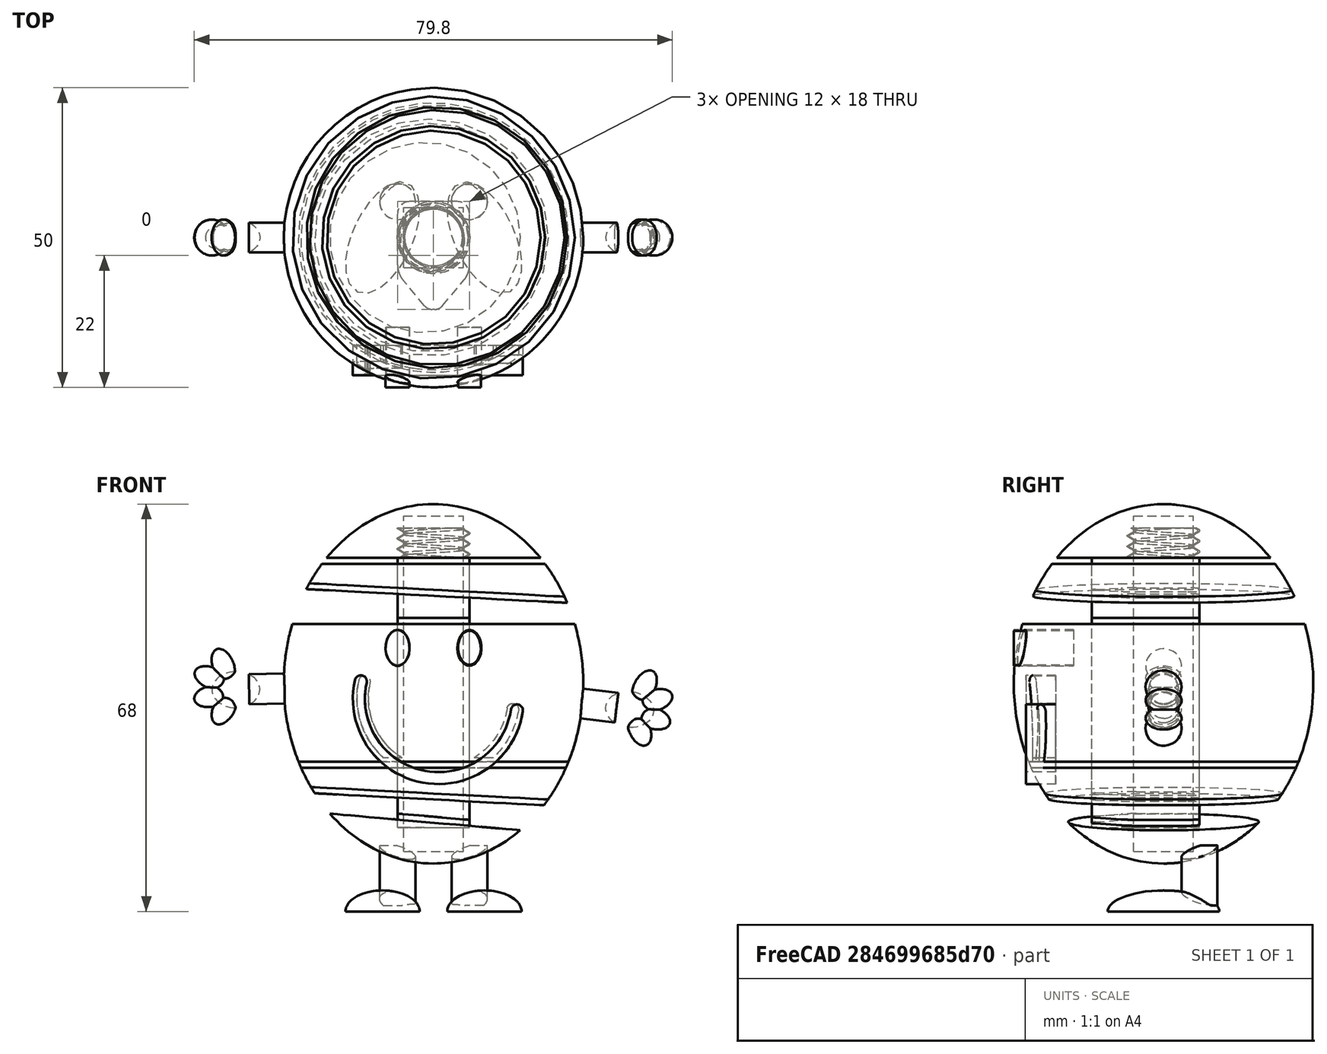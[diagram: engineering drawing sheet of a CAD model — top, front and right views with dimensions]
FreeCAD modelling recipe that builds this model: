
FCSTD DOCUMENT  (FreeCAD 0.21R33771 (Git))
Label: Mr Bump v2
License: All rights reserved
LicenseURL: http://en.wikipedia.org/wiki/All_rights_reserved
objects: Part::FeaturePython×45, Part::Plane×12, Part::MultiFuse×11, Part::Ellipsoid×7, App::DocumentObjectGroup×6, Part::Mirroring×3, Part::Extrusion×3, Part::Box×2, Part::Cylinder×2, Sketcher::SketchObject×2, Part::Part2DObjectPython×2, Part::Face×1, Part::Offset2D×1, Part::Wedge×1, Part::Fillet×1
note: 93 computed .brp shape members not serialized (recipe doc carries the construction recipe); baked Part::Feature solids carry a one-line shape summary decoded from their .brp

FEATURE [Part::Ellipsoid] Ellipsoid
  Angle1 = -90
  Angle2 = 90
  Angle3 = 360
  AttacherType = Attacher::AttachEngine3D
  Radius1 = 30
  Radius2 = 25
  Radius3 = 25
FEATURE [Part::Box] Box  label="Cube"
  AttacherType = Attacher::AttachEngine3D
  Height = 56
  Length = 10
  Placement = pos=(-5,-5,-28) rot=(0,0,1;0rad)
  Width = 10
FEATURE [Part::Cylinder] Cylinder
  Angle = 360
  AttacherType = Attacher::AttachEngine3D
  FirstAngle = 0
  Height = 10
  Placement = pos=(6,6,-37) rot=(0,0,1;0rad)
  Radius = 3
  SecondAngle = 0
FEATURE [Part::Ellipsoid] Ellipsoid006
  Angle1 = -90
  Angle2 = 90
  Angle3 = 360
  AttacherType = Attacher::AttachEngine3D
  Placement = pos=(8.5,0,-38) rot=(0,0,1;0.436332rad)
  Radius1 = 3.5
  Radius2 = 5
  Radius3 = 10
FEATURE [Sketcher::SketchObject] Sketch012
  FullyConstrained = false
  sketch-geometry (4):
    g0: LineSegment StartX=-75.9093 StartY=70.947 StartZ=0 EndX=76.7827 EndY=70.947 EndZ=0
    g1: LineSegment StartX=76.7827 StartY=70.947 StartZ=0 EndX=76.7827 EndY=-70.9765 EndZ=0
    g2: LineSegment StartX=76.7827 StartY=-70.9765 StartZ=0 EndX=-75.9093 EndY=-70.9765 EndZ=0
    g3: LineSegment StartX=-75.9093 StartY=-70.9765 StartZ=0 EndX=-75.9093 EndY=70.947 EndZ=0
  constraints (8):
    c: Coincident(g0,g1)
    c: Coincident(g1,g2)
    c: Coincident(g2,g3)
    c: Coincident(g3,g0)
    c: Horizontal(g0)
    c: Horizontal(g2)
    c: Vertical(g1)
    c: Vertical(g3)
FEATURE [Part::Face] Face012
  FaceMakerClass = Part::FaceMakerBullseye
  Placement = pos=(-7,0,-38) rot=(0,0,1;0rad)
  Sources = -> [Sketch012]
FEATURE [Part::FeaturePython] Slice  # WARN: FeaturePython — macro-defined, semantics opaque (R4)
  Base = -> Ellipsoid006
  Mode = 1
  Tolerance = 0
  Tools = -> [Face012]
FEATURE [Part::FeaturePython] Slice_child0  label="Slice.0"  # WARN: FeaturePython — macro-defined, semantics opaque (R4)
  Base = -> Slice
  FilterType = 1
  Invert = false
  OverrideMaxVal = 0
  WindowFrom = 80
  WindowTo = 100
  items = 0
FEATURE [Part::MultiFuse] Fusion  label="Foot"
  Shapes = -> [Slice_child0,Cylinder]
FEATURE [Part::Cylinder] Cylinder002
  Angle = 360
  AttacherType = Attacher::AttachEngine3D
  FirstAngle = 0
  Height = 8
  Placement = pos=(26,0,0) rot=(0,1,0;1.5708rad)
  Radius = 2.5
  SecondAngle = 0
FEATURE [Part::Ellipsoid] Ellipsoid001
  Angle1 = -90
  Angle2 = 90
  Angle3 = 360
  AttacherType = Attacher::AttachEngine3D
  Placement = pos=(35,0,0) rot=(0,0,1;0rad)
  Radius1 = 3
  Radius2 = 4
  Radius3 = 3
FEATURE [Part::Ellipsoid] Ellipsoid002
  Angle1 = -90
  Angle2 = 90
  Angle3 = 360
  AttacherType = Attacher::AttachEngine3D
  Placement = pos=(37,0,4) rot=(0,1,0;0.349066rad)
  Radius1 = 3
  Radius2 = 1.75
  Radius3 = 3
FEATURE [Part::Ellipsoid] Ellipsoid003
  Angle1 = -90
  Angle2 = 90
  Angle3 = 360
  AttacherType = Attacher::AttachEngine3D
  Placement = pos=(39,0,2) rot=(0,1,0;1.13446rad)
  Radius1 = 3
  Radius2 = 1.75
  Radius3 = 3
FEATURE [Part::Ellipsoid] Ellipsoid004
  Angle1 = -90
  Angle2 = 90
  Angle3 = 360
  AttacherType = Attacher::AttachEngine3D
  Placement = pos=(39,0,-1) rot=(0,1,0;1.74533rad)
  Radius1 = 3
  Radius2 = 1.75
  Radius3 = 3
FEATURE [Part::Ellipsoid] Ellipsoid005
  Angle1 = -90
  Angle2 = 90
  Angle3 = 360
  AttacherType = Attacher::AttachEngine3D
  Placement = pos=(37,0,-3) rot=(0,-1,0;0.523599rad)
  Radius1 = 3
  Radius2 = 1.75
  Radius3 = 3
FEATURE [Part::MultiFuse] Fusion002  label="Hand"
  Placement = pos=(-2,0,0) rot=(0,1,0;0.122173rad)
  Shapes = -> [Cylinder002,Ellipsoid001,Ellipsoid002,Ellipsoid003,Ellipsoid004,Ellipsoid005]
FEATURE [Part::Mirroring] Part__Mirroring  label="Foot (Mirror #1)"
  Base = (1,0,0)
  Normal = (1,0,0)
  Placement = pos=(-2,0,0) rot=(0,0,1;0rad)
  Source = -> Fusion
FEATURE [Part::MultiFuse] Fusion003  label="Feet"
  Shapes = -> [Part__Mirroring,Fusion]
FEATURE [Part::Mirroring] Part__Mirroring001  label="Hand (Mirror #2)"
  Base = (0,0,0)
  Normal = (1,0,-0.05)
  Source = -> Fusion002
FEATURE [Part::MultiFuse] Fusion004  label="Hands"
  Shapes = -> [Fusion002,Part__Mirroring001]
FEATURE [Part::Part2DObjectPython] Ellipse001  # Draft 2D object (typed FeaturePython)
  Area = 18.8496
  FirstAngle = 0
  LastAngle = 0
  MajorRadius = 3
  MakeFace = true
  MinorRadius = 2
  Placement = pos=(6,0,6) rot=(0.57735,-0.57735,0.57735;2.0944rad)
FEATURE [Part::Extrusion] Extrude002  label="Eye Hole Right"
  Base = -> Ellipse001
  Dir = (-1e-16,-1,3e-16)
  DirMode = 2
  FaceMakerClass = Part::FaceMakerBullseye
  LengthFwd = 10
  LengthRev = 0
  Placement = pos=(0,-15,0) rot=(0,0,1;0rad)
  Solid = false
  Symmetric = false
FEATURE [Part::FeaturePython] Clone  label="Uncut Eye"  # Draft clone (typed FeaturePython)
  AttacherType = Attacher::AttachEngine3D
  Fuse = false
  Objects = -> [Extrude002]
  Placement = pos=(0.3,-15,0.3) rot=(0,0,1;0rad)
  Scale = (0.95,1,0.95)
FEATURE [Part::Part2DObjectPython] Ellipse002  # Draft 2D object (typed FeaturePython)
  Area = 18.8496
  FirstAngle = 0
  LastAngle = 0
  MajorRadius = 3
  MakeFace = true
  MinorRadius = 2
  Placement = pos=(7,0,6) rot=(0.57735,-0.57735,0.57735;2.0944rad)
FEATURE [Part::Extrusion] Extrude003  label="Eye Hole Left"
  Base = -> Ellipse002
  Dir = (-2e-16,-1,2e-16)
  DirMode = 2
  FaceMakerClass = Part::FaceMakerBullseye
  LengthFwd = 10
  LengthRev = 0
  Placement = pos=(-13,-15,0) rot=(0,0,1;0rad)
  Solid = false
  Symmetric = false
FEATURE [Sketcher::SketchObject] Sketch005
  FullyConstrained = false
  Placement = pos=(0,0,0) rot=(1,0,0;1.5708rad)
  sketch-geometry (1):
    g0: ArcOfCircle CenterX=0.810583 CenterY=-2.47492 CenterZ=0 NormalX=0 NormalY=0 NormalZ=1 AngleXU=0 Radius=13.2658 StartAngle=2.92236 EndAngle=6.13423
FEATURE [Part::Offset2D] Offset2D
  Fill = false
  Intersection = false
  Join = 0
  Mode = 1
  SelfIntersection = false
  Source = -> Sketch005
  Value = 1
FEATURE [Part::Extrusion] Extrude  label="Mouth Hole"
  Base = -> Offset2D
  Dir = (0,1,-2e-16)
  DirMode = 2
  FaceMakerClass = Part::FaceMakerBullseye
  LengthFwd = 5
  LengthRev = 0
  Placement = pos=(0,-23,0) rot=(0,0,1;0rad)
  Solid = true
  Symmetric = false
FEATURE [Part::Plane] Plane
  AttacherType = Attacher::AttachEngine3D
  Length = 50
  Placement = pos=(-25,-25,-13) rot=(0,0,1;0rad)
  Width = 50
FEATURE [Part::Plane] Plane001
  AttacherType = Attacher::AttachEngine3D
  Length = 50
  Placement = pos=(-25,-25,-14) rot=(0,0,1;0rad)
  Width = 50
FEATURE [Part::Plane] Plane002
  AttacherType = Attacher::AttachEngine3D
  Length = 50
  Placement = pos=(-25,-25,-17) rot=(0,1,0;0.05236rad)
  Width = 50
FEATURE [Part::Plane] Plane003
  AttacherType = Attacher::AttachEngine3D
  Length = 50
  Placement = pos=(-25,-25,-18) rot=(0,1,0;0.05236rad)
  Width = 50
FEATURE [Part::Plane] Plane004
  AttacherType = Attacher::AttachEngine3D
  Length = 50
  Placement = pos=(-25,-25,-20) rot=(0,1,0;0.087266rad)
  Width = 50
FEATURE [Part::Plane] Plane005
  AttacherType = Attacher::AttachEngine3D
  Length = 50
  Placement = pos=(-25,-25,-21) rot=(0,1,0;0.087266rad)
  Width = 50
FEATURE [Part::Plane] Plane006
  AttacherType = Attacher::AttachEngine3D
  Length = 50
  Placement = pos=(-25,-25,10) rot=(0,0,1;0rad)
  Width = 50
FEATURE [Part::Plane] Plane007
  AttacherType = Attacher::AttachEngine3D
  Length = 50
  Placement = pos=(-25,-25,11) rot=(0,0,1;0rad)
  Width = 50
FEATURE [Part::Plane] Plane008
  AttacherType = Attacher::AttachEngine3D
  Length = 50
  Placement = pos=(-25,-25,17) rot=(0,1,0;0.05236rad)
  Width = 50
FEATURE [Part::Plane] Plane009
  AttacherType = Attacher::AttachEngine3D
  Length = 50
  Placement = pos=(-25,-25,16) rot=(0,1,0;0.05236rad)
  Width = 50
FEATURE [Part::Plane] Plane010
  AttacherType = Attacher::AttachEngine3D
  Length = 50
  Placement = pos=(-25,-25,21) rot=(0,0,1;0rad)
  Width = 50
FEATURE [Part::Plane] Plane011
  AttacherType = Attacher::AttachEngine3D
  Length = 50
  Placement = pos=(-25,-25,20) rot=(0,0,1;0rad)
  Width = 50
FEATURE [Part::Box] Box001  label="Cube001"
  AttacherType = Attacher::AttachEngine3D
  Height = 45
  Length = 12
  Placement = pos=(-6,-6,-24) rot=(0,0,1;0rad)
  Width = 12
FEATURE [Part::FeaturePython] ScrewTap  label="M12x5-ScrewTap"  # Fasteners workbench fastener (typed FeaturePython)
  Placement = pos=(0,0,26) rot=(0,0,1;0rad)
  diameter = 11
  diameterCustom = 6
  invert = false
  leftHanded = false
  length = 5
  matchOuter = false
  offset = 0
  pitchCustom = 1
  thread = true
  type = 2
FEATURE [Part::FeaturePython] Clone001  label="Mouth Right"  # WARN: FeaturePython — macro-defined, semantics opaque (R4)
  AttacherType = Attacher::AttachEngine3D
  Fuse = false
  Scale = (0.95,1,0.95)
FEATURE [Part::FeaturePython] Clone002  label="Mouth Left"  # WARN: FeaturePython — macro-defined, semantics opaque (R4)
  AttacherType = Attacher::AttachEngine3D
  Fuse = false
  Scale = (0.95,1,0.95)
FEATURE [Part::FeaturePython] Slice004  # WARN: FeaturePython — macro-defined, semantics opaque (R4)
  Base = -> Clone
  Mode = 1
  Tolerance = 0
  Tools = -> [Ellipsoid]
FEATURE [Part::FeaturePython] Slice004_child0  label="Eye Right"  # WARN: FeaturePython — macro-defined, semantics opaque (R4)
  Base = -> Slice004
  FilterType = 1
  Invert = false
  OverrideMaxVal = 0
  WindowFrom = 80
  WindowTo = 100
  items = 0
FEATURE [Part::FeaturePython] Slice004_child1  label="Slice004.1"  # WARN: FeaturePython — macro-defined, semantics opaque (R4)
  Base = -> Slice004
  FilterType = 1
  Invert = false
  OverrideMaxVal = 0
  WindowFrom = 80
  WindowTo = 100
  items = 1
FEATURE [App::DocumentObjectGroup] GrExplode_Slice004  label="Exploded Slice004"
  Group = -> [Slice004_child1]
FEATURE [App::DocumentObjectGroup] GrExplode_Slice005  label="Exploded Slice005"
FEATURE [Part::Mirroring] Part__Mirroring002  label="Eye Left"
  Base = (0,0,0)
  Normal = (1,0,0)
  Source = -> Slice004_child0
FEATURE [Part::Wedge] Wedge
  AttacherType = Attacher::AttachEngine3D
  Placement = pos=(0,-12,0) rot=(0,0,1;0rad)
  X2max = 6
  X2min = -6
  Xmax = 1
  Xmin = -1
  Ymax = 6
  Ymin = 0
  Z2max = 21
  Z2min = -24
  Zmax = 21
  Zmin = -24
FEATURE [Part::MultiFuse] Fusion010
  Shapes = -> [Wedge,Box001]
FEATURE [Part::Fillet] Fillet
  Base = -> Fusion010
  Edges = 6 edges: [Edge1 r=1.75,Edge3 r=4,Edge6 r=1.75,Edge11 r=2,Edge15 r=4,Edge19 r=2]
FEATURE [Part::MultiFuse] Fusion011  label="Threaded Prismoid"
  Shapes = -> [Fillet,ScrewTap]
FEATURE [Part::FeaturePython] Slice005  # WARN: FeaturePython — macro-defined, semantics opaque (R4)
  Base = -> Ellipsoid
  Mode = 1
  Tolerance = 0
  Tools = -> [Plane011,Extrude002,Extrude003,Extrude,Plane,Plane001,Plane002,Plane003,Plane004,Plane005,Plane006,Plane007,Plane008,Plane009,Plane010,Fusion011]
FEATURE [Part::FeaturePython] Slice005_child0  label="White Bandage 5"  # WARN: FeaturePython — macro-defined, semantics opaque (R4)
  Base = -> Slice005
  FilterType = 1
  Invert = false
  OverrideMaxVal = 0
  WindowFrom = 80
  WindowTo = 100
  items = 0
FEATURE [Part::FeaturePython] Slice005_child1  label="Black Bandage 6"  # WARN: FeaturePython — macro-defined, semantics opaque (R4)
  Base = -> Slice005
  FilterType = 1
  Invert = false
  OverrideMaxVal = 0
  WindowFrom = 80
  WindowTo = 100
  items = 1
FEATURE [Part::FeaturePython] Slice005_child2  label="White Bandage 4"  # WARN: FeaturePython — macro-defined, semantics opaque (R4)
  Base = -> Slice005
  FilterType = 1
  Invert = false
  OverrideMaxVal = 0
  WindowFrom = 80
  WindowTo = 100
  items = 2
FEATURE [Part::FeaturePython] Slice005_child3  label="Slice005.3"  # WARN: FeaturePython — macro-defined, semantics opaque (R4)
  Base = -> Slice005
  FilterType = 1
  Invert = false
  OverrideMaxVal = 0
  WindowFrom = 80
  WindowTo = 100
  items = 3
FEATURE [Part::FeaturePython] Slice005_child4  label="Black Bandage 5"  # WARN: FeaturePython — macro-defined, semantics opaque (R4)
  Base = -> Slice005
  FilterType = 1
  Invert = false
  OverrideMaxVal = 0
  WindowFrom = 80
  WindowTo = 100
  items = 4
FEATURE [Part::FeaturePython] Slice005_child5  label="Slice005.x001"  # WARN: FeaturePython — macro-defined, semantics opaque (R4)
  Base = -> Slice005
  FilterType = 1
  Invert = false
  OverrideMaxVal = 0
  WindowFrom = 80
  WindowTo = 100
  items = 5
FEATURE [Part::FeaturePython] Slice005_child6  label="Slice005.6"  # WARN: FeaturePython — macro-defined, semantics opaque (R4)
  Base = -> Slice005
  FilterType = 1
  Invert = false
  OverrideMaxVal = 0
  WindowFrom = 80
  WindowTo = 100
  items = 6
FEATURE [Part::FeaturePython] Slice005_child7  label="White Bandage 3"  # WARN: FeaturePython — macro-defined, semantics opaque (R4)
  Base = -> Slice005
  FilterType = 1
  Invert = false
  OverrideMaxVal = 0
  WindowFrom = 80
  WindowTo = 100
  items = 7
FEATURE [Part::FeaturePython] Slice005_child8  label="Slice005.8"  # WARN: FeaturePython — macro-defined, semantics opaque (R4)
  Base = -> Slice005
  FilterType = 1
  Invert = false
  OverrideMaxVal = 0
  WindowFrom = 80
  WindowTo = 100
  items = 8
FEATURE [Part::FeaturePython] Slice005_child9  label="Black Bandage 4"  # WARN: FeaturePython — macro-defined, semantics opaque (R4)
  Base = -> Slice005
  FilterType = 1
  Invert = false
  OverrideMaxVal = 0
  WindowFrom = 80
  WindowTo = 100
  items = 9
FEATURE [Part::FeaturePython] Slice005_child10  label="Slice005.10"  # WARN: FeaturePython — macro-defined, semantics opaque (R4)
  Base = -> Slice005
  FilterType = 1
  Invert = false
  OverrideMaxVal = 0
  WindowFrom = 80
  WindowTo = 100
  items = 10
FEATURE [Part::FeaturePython] Slice005_child11  label="Slice005.11"  # WARN: FeaturePython — macro-defined, semantics opaque (R4)
  Base = -> Slice005
  FilterType = 1
  Invert = false
  OverrideMaxVal = 0
  WindowFrom = 80
  WindowTo = 100
  items = 11
FEATURE [Part::MultiFuse] Fusion008  label="Face and Hands"
  Shapes = -> [Fusion004,Slice005_child11]
FEATURE [Part::FeaturePython] Slice005_child12  label="Slice005.12"  # WARN: FeaturePython — macro-defined, semantics opaque (R4)
  Base = -> Slice005
  FilterType = 1
  Invert = false
  OverrideMaxVal = 0
  WindowFrom = 80
  WindowTo = 100
  items = 12
FEATURE [Part::FeaturePython] Slice005_child13  label="Slice005.13"  # WARN: FeaturePython — macro-defined, semantics opaque (R4)
  Base = -> Slice005
  FilterType = 1
  Invert = false
  OverrideMaxVal = 0
  WindowFrom = 80
  WindowTo = 100
  items = 13
FEATURE [Part::FeaturePython] Slice005_child14  label="Slice005.14"  # WARN: FeaturePython — macro-defined, semantics opaque (R4)
  Base = -> Slice005
  FilterType = 1
  Invert = false
  OverrideMaxVal = 0
  WindowFrom = 80
  WindowTo = 100
  items = 14
FEATURE [Part::FeaturePython] Slice005_child15  label="Slice005.15"  # WARN: FeaturePython — macro-defined, semantics opaque (R4)
  Base = -> Slice005
  FilterType = 1
  Invert = false
  OverrideMaxVal = 0
  WindowFrom = 80
  WindowTo = 100
  items = 15
FEATURE [Part::FeaturePython] Slice005_child16  label="Slice005.16"  # WARN: FeaturePython — macro-defined, semantics opaque (R4)
  Base = -> Slice005
  FilterType = 1
  Invert = false
  OverrideMaxVal = 0
  WindowFrom = 80
  WindowTo = 100
  items = 16
FEATURE [Part::FeaturePython] Slice005_child17  label="Slice005.17"  # WARN: FeaturePython — macro-defined, semantics opaque (R4)
  Base = -> Slice005
  FilterType = 1
  Invert = false
  OverrideMaxVal = 0
  WindowFrom = 80
  WindowTo = 100
  items = 17
FEATURE [Part::FeaturePython] Slice005_child18  label="Slice005.18"  # WARN: FeaturePython — macro-defined, semantics opaque (R4)
  Base = -> Slice005
  FilterType = 1
  Invert = false
  OverrideMaxVal = 0
  WindowFrom = 80
  WindowTo = 100
  items = 18
FEATURE [Part::FeaturePython] Slice005_child19  label="Slice005.x"  # WARN: FeaturePython — macro-defined, semantics opaque (R4)
  Base = -> Slice005
  FilterType = 1
  Invert = false
  OverrideMaxVal = 0
  WindowFrom = 80
  WindowTo = 100
  items = 19
FEATURE [Part::FeaturePython] Slice005_child20  label="Slice005.20"  # WARN: FeaturePython — macro-defined, semantics opaque (R4)
  Base = -> Slice005
  FilterType = 1
  Invert = false
  OverrideMaxVal = 0
  WindowFrom = 80
  WindowTo = 100
  items = 20
FEATURE [Part::FeaturePython] Slice005_child21  label="Slice005.21"  # WARN: FeaturePython — macro-defined, semantics opaque (R4)
  Base = -> Slice005
  FilterType = 1
  Invert = false
  OverrideMaxVal = 0
  WindowFrom = 80
  WindowTo = 100
  items = 21
FEATURE [Part::FeaturePython] Slice005_child22  label="Slice005.22"  # WARN: FeaturePython — macro-defined, semantics opaque (R4)
  Base = -> Slice005
  FilterType = 1
  Invert = false
  OverrideMaxVal = 0
  WindowFrom = 80
  WindowTo = 100
  items = 22
FEATURE [Part::FeaturePython] Slice005_child23  label="Slice005.23"  # WARN: FeaturePython — macro-defined, semantics opaque (R4)
  Base = -> Slice005
  FilterType = 1
  Invert = false
  OverrideMaxVal = 0
  WindowFrom = 80
  WindowTo = 100
  items = 23
FEATURE [Part::FeaturePython] Slice005_child24  label="Black Bandage 2"  # WARN: FeaturePython — macro-defined, semantics opaque (R4)
  Base = -> Slice005
  FilterType = 1
  Invert = false
  OverrideMaxVal = 0
  WindowFrom = 80
  WindowTo = 100
  items = 24
FEATURE [Part::FeaturePython] Slice005_child25  label="Slice005.25"  # WARN: FeaturePython — macro-defined, semantics opaque (R4)
  Base = -> Slice005
  FilterType = 1
  Invert = false
  OverrideMaxVal = 0
  WindowFrom = 80
  WindowTo = 100
  items = 25
FEATURE [Part::FeaturePython] Slice005_child26  label="White Bandage 1"  # WARN: FeaturePython — macro-defined, semantics opaque (R4)
  Base = -> Slice005
  FilterType = 1
  Invert = false
  OverrideMaxVal = 0
  WindowFrom = 80
  WindowTo = 100
  items = 26
FEATURE [Part::FeaturePython] Slice005_child27  label="Slice005.27"  # WARN: FeaturePython — macro-defined, semantics opaque (R4)
  Base = -> Slice005
  FilterType = 1
  Invert = false
  OverrideMaxVal = 0
  WindowFrom = 80
  WindowTo = 100
  items = 27
FEATURE [Part::FeaturePython] Slice005_child28  label="Black Bandage 1"  # WARN: FeaturePython — macro-defined, semantics opaque (R4)
  Base = -> Slice005
  FilterType = 1
  Invert = false
  OverrideMaxVal = 0
  WindowFrom = 80
  WindowTo = 100
  items = 28
FEATURE [Part::FeaturePython] Slice005_child29  label="Slice005.29"  # WARN: FeaturePython — macro-defined, semantics opaque (R4)
  Base = -> Slice005
  FilterType = 1
  Invert = false
  OverrideMaxVal = 0
  WindowFrom = 80
  WindowTo = 100
  items = 29
FEATURE [Part::FeaturePython] Slice005_child30  label="Slice005.30"  # WARN: FeaturePython — macro-defined, semantics opaque (R4)
  Base = -> Slice005
  FilterType = 1
  Invert = false
  OverrideMaxVal = 0
  WindowFrom = 80
  WindowTo = 100
  items = 30
FEATURE [Part::FeaturePython] Slice005_child31  label="Slice005.31"  # WARN: FeaturePython — macro-defined, semantics opaque (R4)
  Base = -> Slice005
  FilterType = 1
  Invert = false
  OverrideMaxVal = 0
  WindowFrom = 80
  WindowTo = 100
  items = 31
FEATURE [Part::FeaturePython] Slice005_child32  label="Slice005.32"  # WARN: FeaturePython — macro-defined, semantics opaque (R4)
  Base = -> Slice005
  FilterType = 1
  Invert = false
  OverrideMaxVal = 0
  WindowFrom = 80
  WindowTo = 100
  items = 32
FEATURE [App::DocumentObjectGroup] GrExplode_Slice006  label="Exploded Slice006"
  Group = -> [Slice005_child3,Slice005_child6,Slice005_child8,Slice005_child10,Slice005_child12,Slice005_child14,Slice005_child15,Slice005_child16,Slice005_child17,Slice005_child18,Slice005_child22,Slice005_child25,Slice005_child27,Slice005_child29,Slice005_child31,Slice005_child32,Slice005_child5]
FEATURE [Part::MultiFuse] Fusion012  label="Black Bandage 3"
  Shapes = -> [Slice005_child20,Slice005_child21,Slice005_child13]
FEATURE [App::DocumentObjectGroup] Group002  label="Black"
  Group = -> [Slice004_child0,Clone001,Clone002,Slice005_child28,Slice005_child1,Slice005_child24,Slice005_child9,Fusion012,Slice005_child4]
FEATURE [Part::MultiFuse] Fusion013  label="White Bandage 2"
  Shapes = -> [Slice005_child19,Slice005_child23]
FEATURE [App::DocumentObjectGroup] Group001  label="White"
  Group = -> [Slice005_child26,Slice005_child2,Slice005_child0,Slice005_child7,Fusion013]
FEATURE [Part::FeaturePython] Clone005  label="Fillet001"  # Draft clone (typed FeaturePython)
  AttacherType = Attacher::AttachEngine3D
  Fuse = false
  Objects = -> [Fillet]
  Scale = (1,1,1)
FEATURE [Part::FeaturePython] Clone006  label="M6x5-ScrewTap001"  # Draft clone (typed FeaturePython)
  AttacherType = Attacher::AttachEngine3D
  Fuse = false
  Objects = -> [ScrewTap]
  Placement = pos=(0,0,26) rot=(0,0,1;0rad)
  Scale = (0.95,0.95,1)
FEATURE [Part::MultiFuse] Fusion014  label="Threaded Prismoid002"
  Shapes = -> [Clone006,Clone005]
FEATURE [Part::MultiFuse] Fusion015  label="Feet Body Lower and Rod"
  Shapes = -> [Fusion003,Slice005_child30,Fusion014]
FEATURE [App::DocumentObjectGroup] Group  label="Blue"
  Group = -> [Fusion008,Fusion015]
